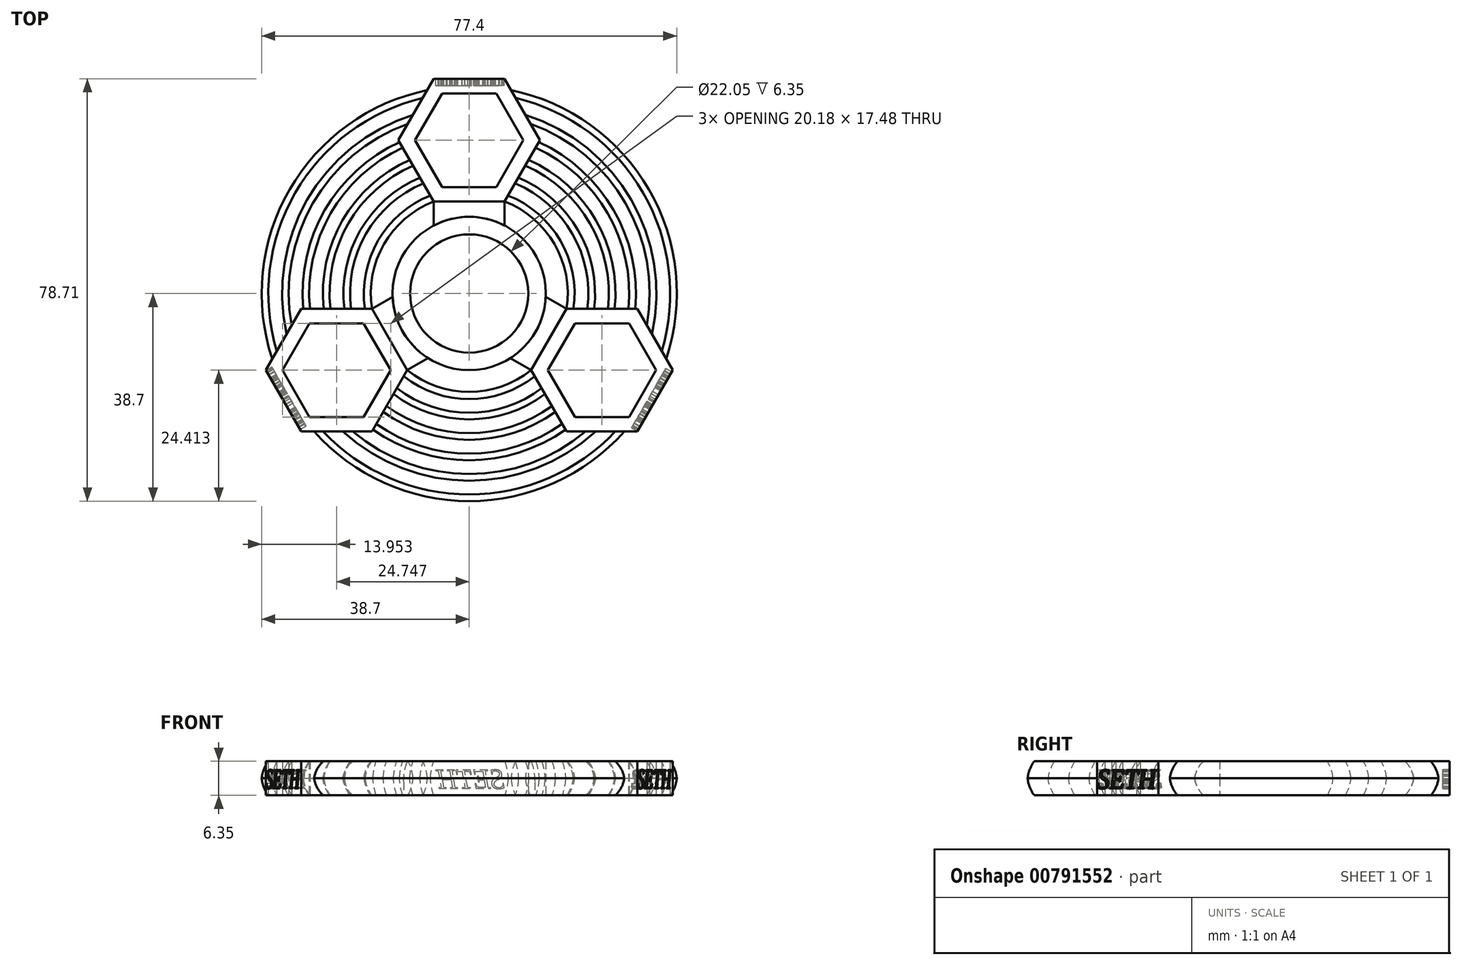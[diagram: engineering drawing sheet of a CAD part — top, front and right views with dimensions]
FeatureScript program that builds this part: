
annotation { "Feature Type Name" : "Feature", "Feature Type Description" : "" }
export const myFeature = defineFeature(function(context is Context, id is Id, definition is map)
    precondition{}
    {
        {
            var Q0;
            Q0=qCreatedBy(makeId("Top.planeOp"),FACE);
            var sketch = newSketch(context, id + "F0", { "sketchPlane" : qUnion([Q0])});
            skCircle(sketch, "E0", {"center": v(0, 0) * mm, "radius": 11.02 * mm});
            skCircle(sketch, "E1", {"center": v(0, 0) * mm, "radius": 14.29 * mm});
            skCircle(sketch, "E2.cCircle", {"center": v(0, 28.58) * mm, "radius": 8.74 * mm, "construction": true});
            skLineSegment(sketch, "E2.0", {"start": v(5.04, 19.84) * mm, "end": v(-5.04, 19.84) * mm});
            skLineSegment(sketch, "E2.1", {"start": v(-5.04, 19.84) * mm, "end": v(-10.09, 28.58) * mm});
            skLineSegment(sketch, "E2.2", {"start": v(-10.09, 28.57) * mm, "end": v(-5.04, 37.31) * mm});
            skLineSegment(sketch, "E2.3", {"start": v(-5.04, 37.31) * mm, "end": v(5.04, 37.31) * mm});
            skLineSegment(sketch, "E2.4", {"start": v(5.04, 37.31) * mm, "end": v(10.09, 28.57) * mm});
            skLineSegment(sketch, "E2.5", {"start": v(10.09, 28.57) * mm, "end": v(5.04, 19.84) * mm});
            skPoint(sketch, "E2.0.midPoint", {"position": v(0, 19.84) * mm});
            skCircle(sketch, "E3.cCircle", {"center": v(0, 28.58) * mm, "radius": 11.43 * mm, "construction": true});
            skLineSegment(sketch, "E3.0", {"start": v(-6.6, 17.15) * mm, "end": v(-13.2, 28.58) * mm});
            skLineSegment(sketch, "E3.1", {"start": v(-13.2, 28.58) * mm, "end": v(-6.6, 40) * mm});
            skLineSegment(sketch, "E3.2", {"start": v(-6.6, 40) * mm, "end": v(6.6, 40) * mm});
            skLineSegment(sketch, "E3.3", {"start": v(6.6, 40) * mm, "end": v(13.2, 28.57) * mm});
            skLineSegment(sketch, "E3.4", {"start": v(13.2, 28.58) * mm, "end": v(6.6, 17.15) * mm});
            skLineSegment(sketch, "E3.5", {"start": v(6.6, 17.15) * mm, "end": v(-6.6, 17.15) * mm});
            skPoint(sketch, "E3.0.midPoint", {"position": v(-9.9, 22.86) * mm});
            skCircle(sketch, "E4.1.0", {"center": v(-24.75, -14.29) * mm, "radius": 8.74 * mm, "construction": true});
            skPoint(sketch, "E4.1.1", {"position": v(-14.85, -20) * mm});
            skLineSegment(sketch, "E4.1.2", {"start": v(-31.35, -2.86) * mm, "end": v(-18.15, -2.86) * mm});
            skLineSegment(sketch, "E4.1.3", {"start": v(-37.94, -14.29) * mm, "end": v(-31.35, -2.86) * mm});
            skLineSegment(sketch, "E4.1.4", {"start": v(-29.8, -23.03) * mm, "end": v(-34.84, -14.29) * mm});
            skCircle(sketch, "E4.1.5", {"center": v(-24.75, -14.29) * mm, "radius": 11.43 * mm, "construction": true});
            skPoint(sketch, "E4.1.6", {"position": v(-17.18, -9.92) * mm});
            skLineSegment(sketch, "E4.1.7", {"start": v(-19.7, -5.55) * mm, "end": v(-14.66, -14.29) * mm});
            skLineSegment(sketch, "E4.1.8", {"start": v(-19.7, -23.03) * mm, "end": v(-29.8, -23.03) * mm});
            skLineSegment(sketch, "E4.1.9", {"start": v(-18.15, -2.86) * mm, "end": v(-11.55, -14.29) * mm});
            skLineSegment(sketch, "E4.1.10", {"start": v(-14.66, -14.29) * mm, "end": v(-19.7, -23.03) * mm});
            skLineSegment(sketch, "E4.1.11", {"start": v(-34.84, -14.29) * mm, "end": v(-29.8, -5.55) * mm});
            skLineSegment(sketch, "E4.1.12", {"start": v(-29.8, -5.55) * mm, "end": v(-19.7, -5.55) * mm});
            skLineSegment(sketch, "E4.1.13", {"start": v(-11.55, -14.29) * mm, "end": v(-18.15, -25.72) * mm});
            skLineSegment(sketch, "E4.1.14", {"start": v(-18.15, -25.72) * mm, "end": v(-31.35, -25.72) * mm});
            skLineSegment(sketch, "E4.1.15", {"start": v(-31.35, -25.72) * mm, "end": v(-37.94, -14.29) * mm});
            skCircle(sketch, "E4.2.0", {"center": v(24.75, -14.29) * mm, "radius": 8.74 * mm, "construction": true});
            skPoint(sketch, "E4.2.1", {"position": v(24.75, -2.86) * mm});
            skLineSegment(sketch, "E4.2.2", {"start": v(18.15, -25.72) * mm, "end": v(11.55, -14.29) * mm});
            skLineSegment(sketch, "E4.2.3", {"start": v(31.35, -25.72) * mm, "end": v(18.15, -25.72) * mm});
            skLineSegment(sketch, "E4.2.4", {"start": v(34.84, -14.29) * mm, "end": v(29.8, -23.03) * mm});
            skCircle(sketch, "E4.2.5", {"center": v(24.75, -14.29) * mm, "radius": 11.43 * mm, "construction": true});
            skPoint(sketch, "E4.2.6", {"position": v(17.18, -9.92) * mm});
            skLineSegment(sketch, "E4.2.7", {"start": v(14.66, -14.29) * mm, "end": v(19.7, -5.55) * mm});
            skLineSegment(sketch, "E4.2.8", {"start": v(29.8, -5.55) * mm, "end": v(34.84, -14.29) * mm});
            skLineSegment(sketch, "E4.2.9", {"start": v(11.55, -14.29) * mm, "end": v(18.15, -2.86) * mm});
            skLineSegment(sketch, "E4.2.10", {"start": v(19.7, -5.55) * mm, "end": v(29.8, -5.55) * mm});
            skLineSegment(sketch, "E4.2.11", {"start": v(29.8, -23.03) * mm, "end": v(19.7, -23.03) * mm});
            skLineSegment(sketch, "E4.2.12", {"start": v(19.7, -23.03) * mm, "end": v(14.66, -14.29) * mm});
            skLineSegment(sketch, "E4.2.13", {"start": v(18.15, -2.86) * mm, "end": v(31.35, -2.86) * mm});
            skLineSegment(sketch, "E4.2.14", {"start": v(31.35, -2.86) * mm, "end": v(37.94, -14.29) * mm});
            skLineSegment(sketch, "E4.2.15", {"start": v(37.94, -14.29) * mm, "end": v(31.35, -25.72) * mm});
            skSolve(sketch);
        }
        {
            var Q0;
            Q0=qCreatedBy(makeId("Top.planeOp"),FACE);
            var sketch = newSketch(context, id + "F1", { "sketchPlane" : qUnion([Q0])});
            skLineSegment(sketch, "E5.0", {"start": v(-10.09, 28.57) * mm, "end": v(-5.04, 37.31) * mm});
            skCircle(sketch, "E5.1", {"center": v(0, 28.58) * mm, "radius": 8.74 * mm});
            skLineSegment(sketch, "E5.2", {"start": v(-5.04, 37.31) * mm, "end": v(5.04, 37.31) * mm});
            skLineSegment(sketch, "E5.3", {"start": v(5.04, 37.31) * mm, "end": v(10.09, 28.57) * mm});
            skLineSegment(sketch, "E5.4", {"start": v(31.35, -2.86) * mm, "end": v(37.94, -14.29) * mm});
            skLineSegment(sketch, "E5.5", {"start": v(-29.8, -5.55) * mm, "end": v(-19.7, -5.55) * mm});
            skCircle(sketch, "E5.6", {"center": v(0, 0) * mm, "radius": 14.29 * mm});
            skCircle(sketch, "E5.7", {"center": v(0, 0) * mm, "radius": 11.02 * mm});
            skLineSegment(sketch, "E5.8", {"start": v(6.6, 17.15) * mm, "end": v(-6.6, 17.15) * mm});
            skLineSegment(sketch, "E5.9", {"start": v(13.2, 28.58) * mm, "end": v(6.6, 17.15) * mm});
            skLineSegment(sketch, "E5.10", {"start": v(6.6, 40) * mm, "end": v(13.2, 28.57) * mm});
            skLineSegment(sketch, "E5.11", {"start": v(-29.8, -23.03) * mm, "end": v(-34.84, -14.29) * mm});
            skLineSegment(sketch, "E5.12", {"start": v(10.09, 28.57) * mm, "end": v(5.04, 19.84) * mm});
            skCircle(sketch, "E5.13", {"center": v(0, 28.58) * mm, "radius": 11.43 * mm});
            skLineSegment(sketch, "E5.14", {"start": v(-13.2, 28.58) * mm, "end": v(-8.65, 36.45) * mm});
            skLineSegment(sketch, "E5.15", {"start": v(-6.6, 40) * mm, "end": v(6.6, 40) * mm});
            skLineSegment(sketch, "E5.16", {"start": v(37.94, -14.29) * mm, "end": v(31.35, -25.72) * mm});
            skLineSegment(sketch, "E5.17", {"start": v(-11.55, -14.29) * mm, "end": v(-18.15, -25.72) * mm});
            skLineSegment(sketch, "E5.18", {"start": v(29.8, -23.03) * mm, "end": v(19.7, -23.03) * mm});
            skLineSegment(sketch, "E5.19", {"start": v(-18.15, -2.86) * mm, "end": v(-11.55, -14.29) * mm});
            skCircle(sketch, "E5.20", {"center": v(-24.75, -14.29) * mm, "radius": 11.43 * mm});
            skLineSegment(sketch, "E5.21", {"start": v(29.8, -5.55) * mm, "end": v(34.84, -14.29) * mm});
            skLineSegment(sketch, "E5.22", {"start": v(-31.35, -25.72) * mm, "end": v(-37.94, -14.29) * mm});
            skCircle(sketch, "E5.23", {"center": v(-24.75, -14.29) * mm, "radius": 8.74 * mm});
            skLineSegment(sketch, "E5.24", {"start": v(31.35, -25.72) * mm, "end": v(18.15, -25.72) * mm});
            skLineSegment(sketch, "E5.25", {"start": v(-18.15, -25.72) * mm, "end": v(-31.35, -25.72) * mm});
            skLineSegment(sketch, "E5.26", {"start": v(19.7, -23.03) * mm, "end": v(14.66, -14.29) * mm});
            skLineSegment(sketch, "E5.27", {"start": v(-14.66, -14.29) * mm, "end": v(-19.7, -23.03) * mm});
            skCircle(sketch, "E5.28", {"center": v(24.75, -14.29) * mm, "radius": 8.74 * mm});
            skLineSegment(sketch, "E5.29", {"start": v(11.55, -14.29) * mm, "end": v(18.15, -2.86) * mm});
            skLineSegment(sketch, "E5.30", {"start": v(-31.35, -2.86) * mm, "end": v(-18.15, -2.86) * mm});
            skLineSegment(sketch, "E5.31", {"start": v(34.84, -14.29) * mm, "end": v(29.8, -23.03) * mm});
            skLineSegment(sketch, "E5.32", {"start": v(18.15, -2.86) * mm, "end": v(31.35, -2.86) * mm});
            skLineSegment(sketch, "E5.33", {"start": v(-34.84, -14.29) * mm, "end": v(-29.8, -5.55) * mm});
            skLineSegment(sketch, "E5.34", {"start": v(-19.7, -23.03) * mm, "end": v(-29.8, -23.03) * mm});
            skLineSegment(sketch, "E5.35", {"start": v(18.15, -25.72) * mm, "end": v(11.55, -14.29) * mm});
            skLineSegment(sketch, "E5.36", {"start": v(-37.94, -14.29) * mm, "end": v(-31.35, -2.86) * mm});
            skCircle(sketch, "E5.37", {"center": v(24.75, -14.29) * mm, "radius": 11.43 * mm});
            skLineSegment(sketch, "E5.38", {"start": v(-6.6, 17.15) * mm, "end": v(-13.2, 28.58) * mm});
            skLineSegment(sketch, "E6", {"start": v(-6.6, 17.15) * mm, "end": v(-6.6, 12.67) * mm});
            skLineSegment(sketch, "E7", {"start": v(6.6, 17.15) * mm, "end": v(6.6, 12.67) * mm});
            skLineSegment(sketch, "E8", {"start": v(18.15, -2.86) * mm, "end": v(14.27, -0.62) * mm});
            skLineSegment(sketch, "E9", {"start": v(-18.15, -2.86) * mm, "end": v(-14.27, -0.62) * mm});
            skLineSegment(sketch, "E10", {"start": v(-11.55, -14.29) * mm, "end": v(-7.67, -12.05) * mm});
            skLineSegment(sketch, "E11", {"start": v(11.55, -14.29) * mm, "end": v(7.67, -12.05) * mm});
            skCircle(sketch, "E12", {"center": v(0, 0) * mm, "radius": 18.37 * mm});
            skCircle(sketch, "E13", {"center": v(0, 0) * mm, "radius": 19.69 * mm});
            skCircle(sketch, "E14", {"center": v(0, 0) * mm, "radius": 22.23 * mm});
            skCircle(sketch, "E15", {"center": v(0, 0) * mm, "radius": 23.5 * mm});
            skCircle(sketch, "E16", {"center": v(0, 0) * mm, "radius": 26.04 * mm});
            skCircle(sketch, "E17", {"center": v(0, 0) * mm, "radius": 27.3 * mm});
            skArc(sketch, "E18", {"start": v(-12.38, 27.16) * mm, "mid": v(0, -29.85) * mm, "end": v(12.38, 27.16) * mm});
            skArc(sketch, "E19", {"start": v(-13.02, 28.26) * mm, "mid": v(0, -31.12) * mm, "end": v(13.02, 28.26) * mm});
            skArc(sketch, "E20", {"start": v(-7.66, 32.77) * mm, "mid": v(-7.67, 32.77) * mm, "end": v(-7.67, 32.77) * mm});
            skArc(sketch, "E21", {"start": v(-6.6, 34.3) * mm, "mid": v(-6.7, 34.27) * mm, "end": v(-6.81, 34.25) * mm});
            skArc(sketch, "E22", {"start": v(-7.79, 37.94) * mm, "mid": v(0, -38.74) * mm, "end": v(7.79, 37.94) * mm});
            skLineSegment(sketch, "E23.trimOffspring", {"start": v(-7.79, 37.94) * mm, "end": v(-6.6, 40) * mm});
            skLineSegment(sketch, "E24", {"start": v(-8.65, 36.45) * mm, "end": v(-7.79, 37.94) * mm});
            skLineSegment(sketch, "E25", {"start": v(-10.09, 28.57) * mm, "end": v(-5.03, 19.82) * mm});
            skLineSegment(sketch, "E26", {"start": v(-5.03, 19.82) * mm, "end": v(5.04, 19.84) * mm});
            skArc(sketch, "E27.trimOffspring", {"start": v(-8.65, 36.45) * mm, "mid": v(0, -37.47) * mm, "end": v(8.65, 36.45) * mm});
            skArc(sketch, "E28.trimOffspring", {"start": v(-10.39, 33.34) * mm, "mid": v(1.95, -34.87) * mm, "end": v(6.6, 34.3) * mm});
            skArc(sketch, "E29.trimOffspring", {"start": v(-11.42, 31.66) * mm, "mid": v(1.96, -33.6) * mm, "end": v(7.66, 32.77) * mm});
            skSolve(sketch);
        }
        {
            var Q0;
            Q0 = qSketchRegion(id + "F0", true);
            var Q1;
            {var subQ5=sQuery(id+"F1.wireOp",EDGE,"E24");Q1=makeQuery(id+"F1.imprint","IMPRINT",FACE,{"disambiguationData":[TD([[makeQuery(id+"F1.imprint","IMPRINT",EDGE,{"derivedFrom":subQ5}),1.0]])]});}
            var Q2;
            {var subQ0=sQuery(id+"F1.wireOp",EDGE,"E29.trimOffspring");var subQ1=sQuery(id+"F1.wireOp",EDGE,"E5.14");var subQ2=makeQuery(id+"F1.imprint","INTERSECT",VERTEX,{"derivedFrom":[subQ1,subQ0]});Q2=makeQuery(id+"F1.imprint","IMPRINT",FACE,{"disambiguationData":[TD([[makeQuery(id+"F1.imprint","IMPRINT",EDGE,{"disambiguationData":[TD([[subQ2,-1.0]])],"derivedFrom":subQ1}),1.0]])]});}
            var Q3;
            {var subQ0=sQuery(id+"F1.wireOp",EDGE,"E19");var subQ1=sQuery(id+"F1.wireOp",EDGE,"E5.30");var subQ2=makeQuery(id+"F1.imprint","INTERSECT",VERTEX,{"derivedFrom":[subQ1,subQ0]});Q3=makeQuery(id+"F1.imprint","IMPRINT",FACE,{"disambiguationData":[TD([[makeQuery(id+"F1.imprint","IMPRINT",EDGE,{"disambiguationData":[TD([[subQ2,-1.0]])],"derivedFrom":subQ1}),1.0]])]});}
            var Q4;
            {var subQ0=sQuery(id+"F1.wireOp",EDGE,"E17");var subQ1=sQuery(id+"F1.wireOp",EDGE,"E5.30");var subQ2=makeQuery(id+"F1.imprint","INTERSECT",VERTEX,{"derivedFrom":[subQ1,subQ0]});Q4=makeQuery(id+"F1.imprint","IMPRINT",FACE,{"disambiguationData":[TD([[makeQuery(id+"F1.imprint","IMPRINT",EDGE,{"disambiguationData":[TD([[subQ2,-1.0]])],"derivedFrom":subQ1}),1.0]])]});}
            var Q5;
            {var subQ0=sQuery(id+"F1.wireOp",EDGE,"E15");var subQ1=sQuery(id+"F1.wireOp",EDGE,"E5.30");var subQ2=makeQuery(id+"F1.imprint","INTERSECT",VERTEX,{"derivedFrom":[subQ1,subQ0]});Q5=makeQuery(id+"F1.imprint","IMPRINT",FACE,{"disambiguationData":[TD([[makeQuery(id+"F1.imprint","IMPRINT",EDGE,{"disambiguationData":[TD([[subQ2,-1.0]])],"derivedFrom":subQ1}),1.0]])]});}
            var Q6;
            {var subQ1=sQuery(id+"F1.wireOp",EDGE,"E5.30");var subQ3=sQuery(id+"F1.wireOp",EDGE,"E13");var subQ4=makeQuery(id+"F1.imprint","INTERSECT",VERTEX,{"derivedFrom":[subQ1,subQ3]});Q6=makeQuery(id+"F1.imprint","IMPRINT",FACE,{"disambiguationData":[TD([[makeQuery(id+"F1.imprint","IMPRINT",EDGE,{"disambiguationData":[TD([[subQ4,1.0]])],"derivedFrom":subQ3}),1.0]])]});}
            var Q7;
            {var subQ0=sQuery(id+"F1.wireOp",EDGE,"E22");var subQ1=sQuery(id+"F1.wireOp",EDGE,"E5.24");var subQ2=makeQuery(id+"F1.imprint","INTERSECT",VERTEX,{"derivedFrom":[subQ1,subQ0]});Q7=makeQuery(id+"F1.imprint","IMPRINT",FACE,{"disambiguationData":[TD([[makeQuery(id+"F1.imprint","IMPRINT",EDGE,{"disambiguationData":[TD([[subQ2,-1.0]])],"derivedFrom":subQ1}),1.0]])]});}
            var Q8;
            {var subQ0=sQuery(id+"F1.wireOp",EDGE,"E28.trimOffspring");var subQ1=sQuery(id+"F1.wireOp",EDGE,"E5.24");var subQ2=makeQuery(id+"F1.imprint","INTERSECT",VERTEX,{"derivedFrom":[subQ1,subQ0]});Q8=makeQuery(id+"F1.imprint","IMPRINT",FACE,{"disambiguationData":[TD([[makeQuery(id+"F1.imprint","IMPRINT",EDGE,{"disambiguationData":[TD([[subQ2,-1.0]])],"derivedFrom":subQ1}),1.0]])]});}
            var Q9;
            {var subQ0=sQuery(id+"F1.wireOp",EDGE,"E18");var subQ1=sQuery(id+"F1.wireOp",EDGE,"E5.17");var subQ2=makeQuery(id+"F1.imprint","INTERSECT",VERTEX,{"derivedFrom":[subQ1,subQ0]});Q9=makeQuery(id+"F1.imprint","IMPRINT",FACE,{"disambiguationData":[TD([[makeQuery(id+"F1.imprint","IMPRINT",EDGE,{"disambiguationData":[TD([[subQ2,-1.0]])],"derivedFrom":subQ1}),1.0]])]});}
            var Q10;
            {var subQ0=sQuery(id+"F1.wireOp",EDGE,"E16");var subQ1=sQuery(id+"F1.wireOp",EDGE,"E5.17");var subQ2=makeQuery(id+"F1.imprint","INTERSECT",VERTEX,{"derivedFrom":[subQ1,subQ0]});Q10=makeQuery(id+"F1.imprint","IMPRINT",FACE,{"disambiguationData":[TD([[makeQuery(id+"F1.imprint","IMPRINT",EDGE,{"disambiguationData":[TD([[subQ2,-1.0]])],"derivedFrom":subQ1}),1.0]])]});}
            var Q11;
            {var subQ0=sQuery(id+"F1.wireOp",EDGE,"E14");var subQ1=sQuery(id+"F1.wireOp",EDGE,"E5.17");var subQ2=makeQuery(id+"F1.imprint","INTERSECT",VERTEX,{"derivedFrom":[subQ1,subQ0]});Q11=makeQuery(id+"F1.imprint","IMPRINT",FACE,{"disambiguationData":[TD([[makeQuery(id+"F1.imprint","IMPRINT",EDGE,{"disambiguationData":[TD([[subQ2,-1.0]])],"derivedFrom":subQ1}),1.0]])]});}
            var Q12;
            {var subQ1=sQuery(id+"F1.wireOp",EDGE,"E5.17");var subQ3=sQuery(id+"F1.wireOp",EDGE,"E13");var subQ4=makeQuery(id+"F1.imprint","INTERSECT",VERTEX,{"derivedFrom":[subQ1,subQ3]});Q12=makeQuery(id+"F1.imprint","IMPRINT",FACE,{"disambiguationData":[TD([[makeQuery(id+"F1.imprint","IMPRINT",EDGE,{"disambiguationData":[TD([[subQ4,-1.0]])],"derivedFrom":subQ3}),1.0]])]});}
            var Q13;
            {var subQ1=sQuery(id+"F1.wireOp",EDGE,"E5.9");var subQ3=sQuery(id+"F1.wireOp",EDGE,"E13");var subQ4=makeQuery(id+"F1.imprint","INTERSECT",VERTEX,{"derivedFrom":[subQ1,subQ3]});Q13=makeQuery(id+"F1.imprint","IMPRINT",FACE,{"disambiguationData":[TD([[makeQuery(id+"F1.imprint","IMPRINT",EDGE,{"disambiguationData":[TD([[subQ4,1.0]])],"derivedFrom":subQ3}),1.0]])]});}
            var Q14;
            {var subQ0=sQuery(id+"F1.wireOp",EDGE,"E15");var subQ1=sQuery(id+"F1.wireOp",EDGE,"E5.9");var subQ2=makeQuery(id+"F1.imprint","INTERSECT",VERTEX,{"derivedFrom":[subQ1,subQ0]});Q14=makeQuery(id+"F1.imprint","IMPRINT",FACE,{"disambiguationData":[TD([[makeQuery(id+"F1.imprint","IMPRINT",EDGE,{"disambiguationData":[TD([[subQ2,-1.0]])],"derivedFrom":subQ1}),1.0]])]});}
            var Q15;
            {var subQ0=sQuery(id+"F1.wireOp",EDGE,"E22");var subQ1=sQuery(id+"F1.wireOp",EDGE,"E5.4");var subQ2=makeQuery(id+"F1.imprint","INTERSECT",VERTEX,{"derivedFrom":[subQ1,subQ0]});Q15=makeQuery(id+"F1.imprint","IMPRINT",FACE,{"disambiguationData":[TD([[makeQuery(id+"F1.imprint","IMPRINT",EDGE,{"disambiguationData":[TD([[subQ2,1.0]])],"derivedFrom":subQ1}),1.0]])]});}
            var Q16;
            {var subQ0=sQuery(id+"F1.wireOp",EDGE,"E29.trimOffspring");var subQ1=sQuery(id+"F1.wireOp",EDGE,"E5.4");var subQ2=makeQuery(id+"F1.imprint","INTERSECT",VERTEX,{"derivedFrom":[subQ1,subQ0]});Q16=makeQuery(id+"F1.imprint","IMPRINT",FACE,{"disambiguationData":[TD([[makeQuery(id+"F1.imprint","IMPRINT",EDGE,{"disambiguationData":[TD([[subQ2,-1.0]])],"derivedFrom":subQ1}),1.0]])]});}
            var Q17;
            {var subQ0=sQuery(id+"F1.wireOp",EDGE,"E17");var subQ1=sQuery(id+"F1.wireOp",EDGE,"E5.9");var subQ2=makeQuery(id+"F1.imprint","INTERSECT",VERTEX,{"derivedFrom":[subQ1,subQ0]});Q17=makeQuery(id+"F1.imprint","IMPRINT",FACE,{"disambiguationData":[TD([[makeQuery(id+"F1.imprint","IMPRINT",EDGE,{"disambiguationData":[TD([[subQ2,-1.0]])],"derivedFrom":subQ1}),1.0]])]});}
            var Q18;
            {var subQ0=sQuery(id+"F1.wireOp",EDGE,"E18");var subQ1=sQuery(id+"F1.wireOp",EDGE,"E5.9");var subQ2=makeQuery(id+"F1.imprint","INTERSECT",VERTEX,{"derivedFrom":[subQ1,subQ0]});Q18=makeQuery(id+"F1.imprint","IMPRINT",FACE,{"disambiguationData":[TD([[makeQuery(id+"F1.imprint","IMPRINT",EDGE,{"disambiguationData":[TD([[subQ2,1.0]])],"derivedFrom":subQ1}),1.0]])]});}
            var Q19;
            {var subQ1=sQuery(id+"F1.wireOp",EDGE,"E8");Q19=makeQuery(id+"F1.imprint","IMPRINT",FACE,{"disambiguationData":[TD([[makeQuery(id+"F1.imprint","IMPRINT",EDGE,{"derivedFrom":subQ1}),1.0]])]});}
            var Q20;
            {var subQ1=sQuery(id+"F1.wireOp",EDGE,"E6");Q20=makeQuery(id+"F1.imprint","IMPRINT",FACE,{"disambiguationData":[TD([[makeQuery(id+"F1.imprint","IMPRINT",EDGE,{"derivedFrom":subQ1}),1.0]])]});}
            var Q21;
            {var subQ0=sQuery(id+"F1.wireOp",EDGE,"E9");Q21=makeQuery(id+"F1.imprint","IMPRINT",FACE,{"disambiguationData":[TD([[makeQuery(id+"F1.imprint","IMPRINT",EDGE,{"derivedFrom":subQ0}),-1.0]])]});}
            extrude(context, id + "F2", {"entities" : qUnion([Q0, Q1, Q2, Q3, Q4, Q5, Q6, Q7, Q8, Q9, Q10, Q11, Q12, Q13, Q14, Q15, Q16, Q17, Q18, Q19, Q20, Q21]), "depth" : 6.35 * mm, "offsetDistance" : 25.4 * mm});
        }
        {
            var Q0;
            {var subQ0=sQuery(id+"F1.wireOp",EDGE,"E22");Q0=makeQuery(id+"F2.opExtrude","CAP_EDGE",EDGE,{"disambiguationData":[OSD([subQ0]),TDD([makeQuery(id+"F1.imprint","IMPRINT",EDGE,{"disambiguationData":[TD([[makeQuery(id+"F1.imprint","INTERSECT",VERTEX,{"derivedFrom":[sQuery(id+"F1.wireOp",EDGE,"E5.24"),subQ0]}),1.0]])],"derivedFrom":subQ0})])],"isStart":false});}
            var Q1;
            {var subQ0=sQuery(id+"F1.wireOp",EDGE,"E28.trimOffspring");Q1=makeQuery(id+"F2.opExtrude","CAP_EDGE",EDGE,{"disambiguationData":[OSD([subQ0]),TDD([makeQuery(id+"F1.imprint","IMPRINT",EDGE,{"disambiguationData":[TD([[makeQuery(id+"F1.imprint","INTERSECT",VERTEX,{"derivedFrom":[sQuery(id+"F1.wireOp",EDGE,"E5.24"),subQ0]}),1.0]])],"derivedFrom":subQ0})])],"isStart":false});}
            var Q2;
            {var subQ0=sQuery(id+"F1.wireOp",EDGE,"E19");Q2=makeQuery(id+"F2.opExtrude","CAP_EDGE",EDGE,{"disambiguationData":[OSD([subQ0]),TDD([makeQuery(id+"F1.imprint","IMPRINT",EDGE,{"disambiguationData":[TD([[makeQuery(id+"F1.imprint","INTERSECT",VERTEX,{"derivedFrom":[sQuery(id+"F1.wireOp",EDGE,"E5.17"),subQ0]}),-1.0]])],"derivedFrom":subQ0})])],"isStart":false});}
            var Q3;
            {var subQ0=sQuery(id+"F1.wireOp",EDGE,"E17");Q3=makeQuery(id+"F2.opExtrude","CAP_EDGE",EDGE,{"disambiguationData":[OSD([subQ0]),TDD([makeQuery(id+"F1.imprint","IMPRINT",EDGE,{"disambiguationData":[TD([[makeQuery(id+"F1.imprint","INTERSECT",VERTEX,{"derivedFrom":[sQuery(id+"F1.wireOp",EDGE,"E5.17"),subQ0]}),-1.0]])],"derivedFrom":subQ0})])],"isStart":false});}
            var Q4;
            {var subQ0=sQuery(id+"F1.wireOp",EDGE,"E15");Q4=makeQuery(id+"F2.opExtrude","CAP_EDGE",EDGE,{"disambiguationData":[OSD([subQ0]),TDD([makeQuery(id+"F1.imprint","IMPRINT",EDGE,{"disambiguationData":[TD([[makeQuery(id+"F1.imprint","INTERSECT",VERTEX,{"derivedFrom":[sQuery(id+"F1.wireOp",EDGE,"E5.17"),subQ0]}),-1.0]])],"derivedFrom":subQ0})])],"isStart":false});}
            var Q5;
            {var subQ0=sQuery(id+"F1.wireOp",EDGE,"E13");Q5=makeQuery(id+"F2.opExtrude","CAP_EDGE",EDGE,{"disambiguationData":[OSD([subQ0]),TDD([makeQuery(id+"F1.imprint","IMPRINT",EDGE,{"disambiguationData":[TD([[makeQuery(id+"F1.imprint","INTERSECT",VERTEX,{"derivedFrom":[sQuery(id+"F1.wireOp",EDGE,"E5.17"),subQ0]}),-1.0]])],"derivedFrom":subQ0})])],"isStart":false});}
            var Q6;
            {var subQ0=sQuery(id+"F1.wireOp",EDGE,"E22");Q6=makeQuery(id+"F2.opExtrude","CAP_EDGE",EDGE,{"disambiguationData":[OSD([subQ0]),TDD([makeQuery(id+"F1.imprint","IMPRINT",EDGE,{"disambiguationData":[TD([[makeQuery(id+"F1.imprint","INTERSECT",VERTEX,{"derivedFrom":[sQuery(id+"F1.wireOp",EDGE,"E5.10"),subQ0]}),1.0]])],"derivedFrom":subQ0})])],"isStart":false});}
            var Q7;
            {var subQ0=sQuery(id+"F1.wireOp",EDGE,"E28.trimOffspring");Q7=makeQuery(id+"F2.opExtrude","CAP_EDGE",EDGE,{"disambiguationData":[OSD([subQ0]),TDD([makeQuery(id+"F1.imprint","IMPRINT",EDGE,{"disambiguationData":[TD([[makeQuery(id+"F1.imprint","INTERSECT",VERTEX,{"derivedFrom":[sQuery(id+"F1.wireOp",EDGE,"E5.4"),subQ0]}),-1.0]])],"derivedFrom":subQ0})])],"isStart":false});}
            var Q8;
            {var subQ0=sQuery(id+"F1.wireOp",EDGE,"E19");Q8=makeQuery(id+"F2.opExtrude","CAP_EDGE",EDGE,{"disambiguationData":[OSD([subQ0]),TDD([makeQuery(id+"F1.imprint","IMPRINT",EDGE,{"disambiguationData":[TD([[makeQuery(id+"F1.imprint","INTERSECT",VERTEX,{"derivedFrom":[sQuery(id+"F1.wireOp",EDGE,"E5.9"),subQ0]}),1.0]])],"derivedFrom":subQ0})])],"isStart":false});}
            var Q9;
            {var subQ0=sQuery(id+"F1.wireOp",EDGE,"E17");Q9=makeQuery(id+"F2.opExtrude","CAP_EDGE",EDGE,{"disambiguationData":[OSD([subQ0]),TDD([makeQuery(id+"F1.imprint","IMPRINT",EDGE,{"disambiguationData":[TD([[makeQuery(id+"F1.imprint","INTERSECT",VERTEX,{"derivedFrom":[sQuery(id+"F1.wireOp",EDGE,"E5.9"),subQ0]}),1.0]])],"derivedFrom":subQ0})])],"isStart":false});}
            var Q10;
            {var subQ0=sQuery(id+"F1.wireOp",EDGE,"E15");Q10=makeQuery(id+"F2.opExtrude","CAP_EDGE",EDGE,{"disambiguationData":[OSD([subQ0]),TDD([makeQuery(id+"F1.imprint","IMPRINT",EDGE,{"disambiguationData":[TD([[makeQuery(id+"F1.imprint","INTERSECT",VERTEX,{"derivedFrom":[sQuery(id+"F1.wireOp",EDGE,"E5.9"),subQ0]}),1.0]])],"derivedFrom":subQ0})])],"isStart":false});}
            var Q11;
            {var subQ0=sQuery(id+"F1.wireOp",EDGE,"E13");Q11=makeQuery(id+"F2.opExtrude","CAP_EDGE",EDGE,{"disambiguationData":[OSD([subQ0]),TDD([makeQuery(id+"F1.imprint","IMPRINT",EDGE,{"disambiguationData":[TD([[makeQuery(id+"F1.imprint","INTERSECT",VERTEX,{"derivedFrom":[sQuery(id+"F1.wireOp",EDGE,"E5.9"),subQ0]}),1.0]])],"derivedFrom":subQ0})])],"isStart":false});}
            var Q12;
            {var subQ0=sQuery(id+"F1.wireOp",EDGE,"E22");Q12=makeQuery(id+"F2.opExtrude","CAP_EDGE",EDGE,{"disambiguationData":[OSD([subQ0]),TDD([makeQuery(id+"F1.imprint","IMPRINT",EDGE,{"disambiguationData":[TD([[makeQuery(id+"F1.imprint","INTERSECT",VERTEX,{"derivedFrom":[sQuery(id+"F1.wireOp",EDGE,"E5.36"),subQ0]}),1.0]])],"derivedFrom":subQ0})])],"isStart":false});}
            var Q13;
            {var subQ0=sQuery(id+"F1.wireOp",EDGE,"E28.trimOffspring");Q13=makeQuery(id+"F2.opExtrude","CAP_EDGE",EDGE,{"disambiguationData":[OSD([subQ0]),TDD([makeQuery(id+"F1.imprint","IMPRINT",EDGE,{"disambiguationData":[TD([[makeQuery(id+"F1.imprint","INTERSECT",VERTEX,{"derivedFrom":[sQuery(id+"F1.wireOp",EDGE,"E5.14"),subQ0]}),-1.0]])],"derivedFrom":subQ0})])],"isStart":false});}
            var Q14;
            {var subQ0=sQuery(id+"F1.wireOp",EDGE,"E19");Q14=makeQuery(id+"F2.opExtrude","CAP_EDGE",EDGE,{"disambiguationData":[OSD([subQ0]),TDD([makeQuery(id+"F1.imprint","IMPRINT",EDGE,{"disambiguationData":[TD([[makeQuery(id+"F1.imprint","INTERSECT",VERTEX,{"derivedFrom":[sQuery(id+"F1.wireOp",EDGE,"E5.38"),subQ0]}),-1.0]])],"derivedFrom":subQ0})])],"isStart":false});}
            var Q15;
            {var subQ0=sQuery(id+"F1.wireOp",EDGE,"E17");Q15=makeQuery(id+"F2.opExtrude","CAP_EDGE",EDGE,{"disambiguationData":[OSD([subQ0]),TDD([makeQuery(id+"F1.imprint","IMPRINT",EDGE,{"disambiguationData":[TD([[makeQuery(id+"F1.imprint","INTERSECT",VERTEX,{"derivedFrom":[sQuery(id+"F1.wireOp",EDGE,"E5.30"),subQ0]}),1.0]])],"derivedFrom":subQ0})])],"isStart":false});}
            var Q16;
            {var subQ0=sQuery(id+"F1.wireOp",EDGE,"E15");Q16=makeQuery(id+"F2.opExtrude","CAP_EDGE",EDGE,{"disambiguationData":[OSD([subQ0]),TDD([makeQuery(id+"F1.imprint","IMPRINT",EDGE,{"disambiguationData":[TD([[makeQuery(id+"F1.imprint","INTERSECT",VERTEX,{"derivedFrom":[sQuery(id+"F1.wireOp",EDGE,"E5.30"),subQ0]}),1.0]])],"derivedFrom":subQ0})])],"isStart":false});}
            var Q17;
            {var subQ0=sQuery(id+"F1.wireOp",EDGE,"E22");Q17=makeQuery(id+"F2.opExtrude","CAP_EDGE",EDGE,{"disambiguationData":[OSD([subQ0]),TDD([makeQuery(id+"F1.imprint","IMPRINT",EDGE,{"disambiguationData":[TD([[makeQuery(id+"F1.imprint","INTERSECT",VERTEX,{"derivedFrom":[sQuery(id+"F1.wireOp",EDGE,"E5.10"),subQ0]}),1.0]])],"derivedFrom":subQ0})])],"isStart":true});}
            var Q18;
            {var subQ0=sQuery(id+"F1.wireOp",EDGE,"E28.trimOffspring");Q18=makeQuery(id+"F2.opExtrude","CAP_EDGE",EDGE,{"disambiguationData":[OSD([subQ0]),TDD([makeQuery(id+"F1.imprint","IMPRINT",EDGE,{"disambiguationData":[TD([[makeQuery(id+"F1.imprint","INTERSECT",VERTEX,{"derivedFrom":[sQuery(id+"F1.wireOp",EDGE,"E5.4"),subQ0]}),-1.0]])],"derivedFrom":subQ0})])],"isStart":true});}
            var Q19;
            {var subQ0=sQuery(id+"F1.wireOp",EDGE,"E19");Q19=makeQuery(id+"F2.opExtrude","CAP_EDGE",EDGE,{"disambiguationData":[OSD([subQ0]),TDD([makeQuery(id+"F1.imprint","IMPRINT",EDGE,{"disambiguationData":[TD([[makeQuery(id+"F1.imprint","INTERSECT",VERTEX,{"derivedFrom":[sQuery(id+"F1.wireOp",EDGE,"E5.9"),subQ0]}),1.0]])],"derivedFrom":subQ0})])],"isStart":true});}
            var Q20;
            {var subQ0=sQuery(id+"F1.wireOp",EDGE,"E17");Q20=makeQuery(id+"F2.opExtrude","CAP_EDGE",EDGE,{"disambiguationData":[OSD([subQ0]),TDD([makeQuery(id+"F1.imprint","IMPRINT",EDGE,{"disambiguationData":[TD([[makeQuery(id+"F1.imprint","INTERSECT",VERTEX,{"derivedFrom":[sQuery(id+"F1.wireOp",EDGE,"E5.9"),subQ0]}),1.0]])],"derivedFrom":subQ0})])],"isStart":true});}
            var Q21;
            {var subQ0=sQuery(id+"F1.wireOp",EDGE,"E15");Q21=makeQuery(id+"F2.opExtrude","CAP_EDGE",EDGE,{"disambiguationData":[OSD([subQ0]),TDD([makeQuery(id+"F1.imprint","IMPRINT",EDGE,{"disambiguationData":[TD([[makeQuery(id+"F1.imprint","INTERSECT",VERTEX,{"derivedFrom":[sQuery(id+"F1.wireOp",EDGE,"E5.9"),subQ0]}),1.0]])],"derivedFrom":subQ0})])],"isStart":true});}
            var Q22;
            {var subQ0=sQuery(id+"F1.wireOp",EDGE,"E13");Q22=makeQuery(id+"F2.opExtrude","CAP_EDGE",EDGE,{"disambiguationData":[OSD([subQ0]),TDD([makeQuery(id+"F1.imprint","IMPRINT",EDGE,{"disambiguationData":[TD([[makeQuery(id+"F1.imprint","INTERSECT",VERTEX,{"derivedFrom":[sQuery(id+"F1.wireOp",EDGE,"E5.9"),subQ0]}),1.0]])],"derivedFrom":subQ0})])],"isStart":true});}
            var Q23;
            {var subQ0=sQuery(id+"F1.wireOp",EDGE,"E22");Q23=makeQuery(id+"F2.opExtrude","CAP_EDGE",EDGE,{"disambiguationData":[OSD([subQ0]),TDD([makeQuery(id+"F1.imprint","IMPRINT",EDGE,{"disambiguationData":[TD([[makeQuery(id+"F1.imprint","INTERSECT",VERTEX,{"derivedFrom":[sQuery(id+"F1.wireOp",EDGE,"E5.24"),subQ0]}),1.0]])],"derivedFrom":subQ0})])],"isStart":true});}
            var Q24;
            {var subQ0=sQuery(id+"F1.wireOp",EDGE,"E28.trimOffspring");Q24=makeQuery(id+"F2.opExtrude","CAP_EDGE",EDGE,{"disambiguationData":[OSD([subQ0]),TDD([makeQuery(id+"F1.imprint","IMPRINT",EDGE,{"disambiguationData":[TD([[makeQuery(id+"F1.imprint","INTERSECT",VERTEX,{"derivedFrom":[sQuery(id+"F1.wireOp",EDGE,"E5.24"),subQ0]}),1.0]])],"derivedFrom":subQ0})])],"isStart":true});}
            var Q25;
            {var subQ0=sQuery(id+"F1.wireOp",EDGE,"E19");Q25=makeQuery(id+"F2.opExtrude","CAP_EDGE",EDGE,{"disambiguationData":[OSD([subQ0]),TDD([makeQuery(id+"F1.imprint","IMPRINT",EDGE,{"disambiguationData":[TD([[makeQuery(id+"F1.imprint","INTERSECT",VERTEX,{"derivedFrom":[sQuery(id+"F1.wireOp",EDGE,"E5.17"),subQ0]}),-1.0]])],"derivedFrom":subQ0})])],"isStart":true});}
            var Q26;
            {var subQ0=sQuery(id+"F1.wireOp",EDGE,"E17");Q26=makeQuery(id+"F2.opExtrude","CAP_EDGE",EDGE,{"disambiguationData":[OSD([subQ0]),TDD([makeQuery(id+"F1.imprint","IMPRINT",EDGE,{"disambiguationData":[TD([[makeQuery(id+"F1.imprint","INTERSECT",VERTEX,{"derivedFrom":[sQuery(id+"F1.wireOp",EDGE,"E5.17"),subQ0]}),-1.0]])],"derivedFrom":subQ0})])],"isStart":true});}
            var Q27;
            {var subQ0=sQuery(id+"F1.wireOp",EDGE,"E15");Q27=makeQuery(id+"F2.opExtrude","CAP_EDGE",EDGE,{"disambiguationData":[OSD([subQ0]),TDD([makeQuery(id+"F1.imprint","IMPRINT",EDGE,{"disambiguationData":[TD([[makeQuery(id+"F1.imprint","INTERSECT",VERTEX,{"derivedFrom":[sQuery(id+"F1.wireOp",EDGE,"E5.17"),subQ0]}),-1.0]])],"derivedFrom":subQ0})])],"isStart":true});}
            var Q28;
            {var subQ0=sQuery(id+"F1.wireOp",EDGE,"E13");Q28=makeQuery(id+"F2.opExtrude","CAP_EDGE",EDGE,{"disambiguationData":[OSD([subQ0]),TDD([makeQuery(id+"F1.imprint","IMPRINT",EDGE,{"disambiguationData":[TD([[makeQuery(id+"F1.imprint","INTERSECT",VERTEX,{"derivedFrom":[sQuery(id+"F1.wireOp",EDGE,"E5.30"),subQ0]}),1.0]])],"derivedFrom":subQ0})])],"isStart":true});}
            var Q29;
            {var subQ0=sQuery(id+"F1.wireOp",EDGE,"E15");Q29=makeQuery(id+"F2.opExtrude","CAP_EDGE",EDGE,{"disambiguationData":[OSD([subQ0]),TDD([makeQuery(id+"F1.imprint","IMPRINT",EDGE,{"disambiguationData":[TD([[makeQuery(id+"F1.imprint","INTERSECT",VERTEX,{"derivedFrom":[sQuery(id+"F1.wireOp",EDGE,"E5.30"),subQ0]}),1.0]])],"derivedFrom":subQ0})])],"isStart":true});}
            var Q30;
            {var subQ0=sQuery(id+"F1.wireOp",EDGE,"E17");Q30=makeQuery(id+"F2.opExtrude","CAP_EDGE",EDGE,{"disambiguationData":[OSD([subQ0]),TDD([makeQuery(id+"F1.imprint","IMPRINT",EDGE,{"disambiguationData":[TD([[makeQuery(id+"F1.imprint","INTERSECT",VERTEX,{"derivedFrom":[sQuery(id+"F1.wireOp",EDGE,"E5.30"),subQ0]}),1.0]])],"derivedFrom":subQ0})])],"isStart":true});}
            var Q31;
            {var subQ0=sQuery(id+"F1.wireOp",EDGE,"E19");Q31=makeQuery(id+"F2.opExtrude","CAP_EDGE",EDGE,{"disambiguationData":[OSD([subQ0]),TDD([makeQuery(id+"F1.imprint","IMPRINT",EDGE,{"disambiguationData":[TD([[makeQuery(id+"F1.imprint","INTERSECT",VERTEX,{"derivedFrom":[sQuery(id+"F1.wireOp",EDGE,"E5.38"),subQ0]}),-1.0]])],"derivedFrom":subQ0})])],"isStart":true});}
            var Q32;
            {var subQ0=sQuery(id+"F1.wireOp",EDGE,"E28.trimOffspring");Q32=makeQuery(id+"F2.opExtrude","CAP_EDGE",EDGE,{"disambiguationData":[OSD([subQ0]),TDD([makeQuery(id+"F1.imprint","IMPRINT",EDGE,{"disambiguationData":[TD([[makeQuery(id+"F1.imprint","INTERSECT",VERTEX,{"derivedFrom":[sQuery(id+"F1.wireOp",EDGE,"E5.14"),subQ0]}),-1.0]])],"derivedFrom":subQ0})])],"isStart":true});}
            var Q33;
            {var subQ0=sQuery(id+"F1.wireOp",EDGE,"E22");Q33=makeQuery(id+"F2.opExtrude","CAP_EDGE",EDGE,{"disambiguationData":[OSD([subQ0]),TDD([makeQuery(id+"F1.imprint","IMPRINT",EDGE,{"disambiguationData":[TD([[makeQuery(id+"F1.imprint","INTERSECT",VERTEX,{"derivedFrom":[sQuery(id+"F1.wireOp",EDGE,"E5.36"),subQ0]}),1.0]])],"derivedFrom":subQ0})])],"isStart":true});}
            var Q34;
            {var subQ0=sQuery(id+"F1.wireOp",EDGE,"E13");Q34=makeQuery(id+"F2.opExtrude","CAP_EDGE",EDGE,{"disambiguationData":[OSD([subQ0]),TDD([makeQuery(id+"F1.imprint","IMPRINT",EDGE,{"disambiguationData":[TD([[makeQuery(id+"F1.imprint","INTERSECT",VERTEX,{"derivedFrom":[sQuery(id+"F1.wireOp",EDGE,"E5.30"),subQ0]}),1.0]])],"derivedFrom":subQ0})])],"isStart":false});}
            fillet(context, id + "F3", {"entities" : qUnion([Q0, Q1, Q2, Q3, Q4, Q5, Q6, Q7, Q8, Q9, Q10, Q11, Q12, Q13, Q14, Q15, Q16, Q17, Q18, Q19, Q20, Q21, Q22, Q23, Q24, Q25, Q26, Q27, Q28, Q29, Q30, Q31, Q32, Q33, Q34]), "radius" : 6.35 * mm, "tangentPropagation" : true, "allowEdgeOverflow" : false});
        }
        {
            var Q0;
            Q0=makeQuery(id+"F2.opExtrude","SWEPT_FACE",FACE,{"disambiguationData":[OSD([sQuery(id+"F0.wireOp",EDGE,"E4.1.15")])]});
            var sketch = newSketch(context, id + "F4", { "sketchPlane" : qUnion([Q0])});
            skText(sketch, "E30", { "text": "SETH", "fontName": "Tinos-Italic.ttf"});
            skLineSegment(sketch, "E31", {"start": v(-6.6, 5.09) * mm, "end": v(-6.6, 6.35) * mm});
            skLineSegment(sketch, "E32", {"start": v(-6.6, 1.28) * mm, "end": v(-6.6, 0) * mm});
            const initialGuessF4  = {"E30": [-0.0066, 0.00128, 1, 0, 0.0038]};
            skSetInitialGuess(sketch, initialGuessF4);
            skSolve(sketch);
        }
        {
            var Q0;
            Q0=makeQuery(id+"F2.opExtrude","SWEPT_FACE",FACE,{"disambiguationData":[OSD([sQuery(id+"F0.wireOp",EDGE,"E3.2")])]});
            var sketch = newSketch(context, id + "F5", { "sketchPlane" : qUnion([Q0])});
            skText(sketch, "E33", { "text": "SETH", "fontName": "Tinos-Italic.ttf"});
            skLineSegment(sketch, "E34", {"start": v(-6.6, 6.35) * mm, "end": v(-6.6, 5.08) * mm});
            skLineSegment(sketch, "E35", {"start": v(-6.6, 1.27) * mm, "end": v(-6.6, 0) * mm});
            const initialGuessF5  = {"E33": [-0.0066, 0.00127, 1, 0, 0.0038]};
            skSetInitialGuess(sketch, initialGuessF5);
            skSolve(sketch);
        }
        {
            var Q0;
            Q0=makeQuery(id+"F2.opExtrude","SWEPT_FACE",FACE,{"disambiguationData":[OSD([sQuery(id+"F0.wireOp",EDGE,"E4.2.15")])]});
            var sketch = newSketch(context, id + "F6", { "sketchPlane" : qUnion([Q0])});
            skText(sketch, "E36", { "text": "SETH", "fontName": "Tinos-Italic.ttf"});
            const initialGuessF6  = {"E36": [-0.0066, 0.00127, 1, 0, 0.0038]};
            skSetInitialGuess(sketch, initialGuessF6);
            skSolve(sketch);
        }
        {
            var Q0;
            Q0=makeQuery(id+"F6.imprint","IMPRINT",FACE,{"disambiguationData":[TD([[makeQuery(id+"F6.imprint","IMPRINT",EDGE,{"derivedFrom":sQuery(id+"F6.wireOp",EDGE,"E36.sketch_text.stroke-0")}),-1.0]])]});
            var Q1;
            Q1=makeQuery(id+"F6.imprint","IMPRINT",FACE,{"disambiguationData":[TD([[makeQuery(id+"F6.imprint","IMPRINT",EDGE,{"derivedFrom":sQuery(id+"F6.wireOp",EDGE,"E36.sketch_text.stroke-35")}),-1.0]])]});
            var Q2;
            Q2=makeQuery(id+"F6.imprint","IMPRINT",FACE,{"disambiguationData":[TD([[makeQuery(id+"F6.imprint","IMPRINT",EDGE,{"derivedFrom":sQuery(id+"F6.wireOp",EDGE,"E36.sketch_text.stroke-61")}),-1.0]])]});
            var Q3;
            Q3=makeQuery(id+"F6.imprint","IMPRINT",FACE,{"disambiguationData":[TD([[makeQuery(id+"F6.imprint","IMPRINT",EDGE,{"derivedFrom":sQuery(id+"F6.wireOp",EDGE,"E36.sketch_text.stroke-79")}),-1.0]])]});
            extrude(context, id + "F7", {"entities" : qUnion([Q0, Q1, Q2, Q3]), "operationType" : NewBodyOperationType.REMOVE, "oppositeDirection" : true, "depth" : 1.27 * mm, "offsetDistance" : 25.4 * mm});
        }
        {
            var Q0;
            Q0=makeQuery(id+"F4.imprint","IMPRINT",FACE,{"disambiguationData":[TD([[makeQuery(id+"F4.imprint","IMPRINT",EDGE,{"derivedFrom":sQuery(id+"F4.wireOp",EDGE,"E30.sketch_text.stroke-35")}),-1.0]])]});
            var Q1;
            Q1=makeQuery(id+"F4.imprint","IMPRINT",FACE,{"disambiguationData":[TD([[makeQuery(id+"F4.imprint","IMPRINT",EDGE,{"derivedFrom":sQuery(id+"F4.wireOp",EDGE,"E30.sketch_text.stroke-0")}),-1.0]])]});
            var Q2;
            Q2=makeQuery(id+"F4.imprint","IMPRINT",FACE,{"disambiguationData":[TD([[makeQuery(id+"F4.imprint","IMPRINT",EDGE,{"derivedFrom":sQuery(id+"F4.wireOp",EDGE,"E30.sketch_text.stroke-79")}),-1.0]])]});
            var Q3;
            Q3=makeQuery(id+"F4.imprint","IMPRINT",FACE,{"disambiguationData":[TD([[makeQuery(id+"F4.imprint","IMPRINT",EDGE,{"derivedFrom":sQuery(id+"F4.wireOp",EDGE,"E30.sketch_text.stroke-61")}),-1.0]])]});
            extrude(context, id + "F8", {"entities" : qUnion([Q0, Q1, Q2, Q3]), "operationType" : NewBodyOperationType.REMOVE, "oppositeDirection" : true, "depth" : 1.27 * mm, "offsetDistance" : 25.4 * mm});
        }
        {
            var Q0;
            Q0=makeQuery(id+"F5.imprint","IMPRINT",FACE,{"disambiguationData":[TD([[makeQuery(id+"F5.imprint","IMPRINT",EDGE,{"derivedFrom":sQuery(id+"F5.wireOp",EDGE,"E33.sketch_text.stroke-0")}),-1.0]])]});
            var Q1;
            Q1=makeQuery(id+"F5.imprint","IMPRINT",FACE,{"disambiguationData":[TD([[makeQuery(id+"F5.imprint","IMPRINT",EDGE,{"derivedFrom":sQuery(id+"F5.wireOp",EDGE,"E33.sketch_text.stroke-35")}),-1.0]])]});
            var Q2;
            Q2=makeQuery(id+"F5.imprint","IMPRINT",FACE,{"disambiguationData":[TD([[makeQuery(id+"F5.imprint","IMPRINT",EDGE,{"derivedFrom":sQuery(id+"F5.wireOp",EDGE,"E33.sketch_text.stroke-61")}),-1.0]])]});
            var Q3;
            Q3=makeQuery(id+"F5.imprint","IMPRINT",FACE,{"disambiguationData":[TD([[makeQuery(id+"F5.imprint","IMPRINT",EDGE,{"derivedFrom":sQuery(id+"F5.wireOp",EDGE,"E33.sketch_text.stroke-79")}),-1.0]])]});
            extrude(context, id + "F9", {"entities" : qUnion([Q0, Q1, Q2, Q3]), "operationType" : NewBodyOperationType.REMOVE, "oppositeDirection" : true, "depth" : 1.27 * mm, "offsetDistance" : 25.4 * mm});
        }
    });
